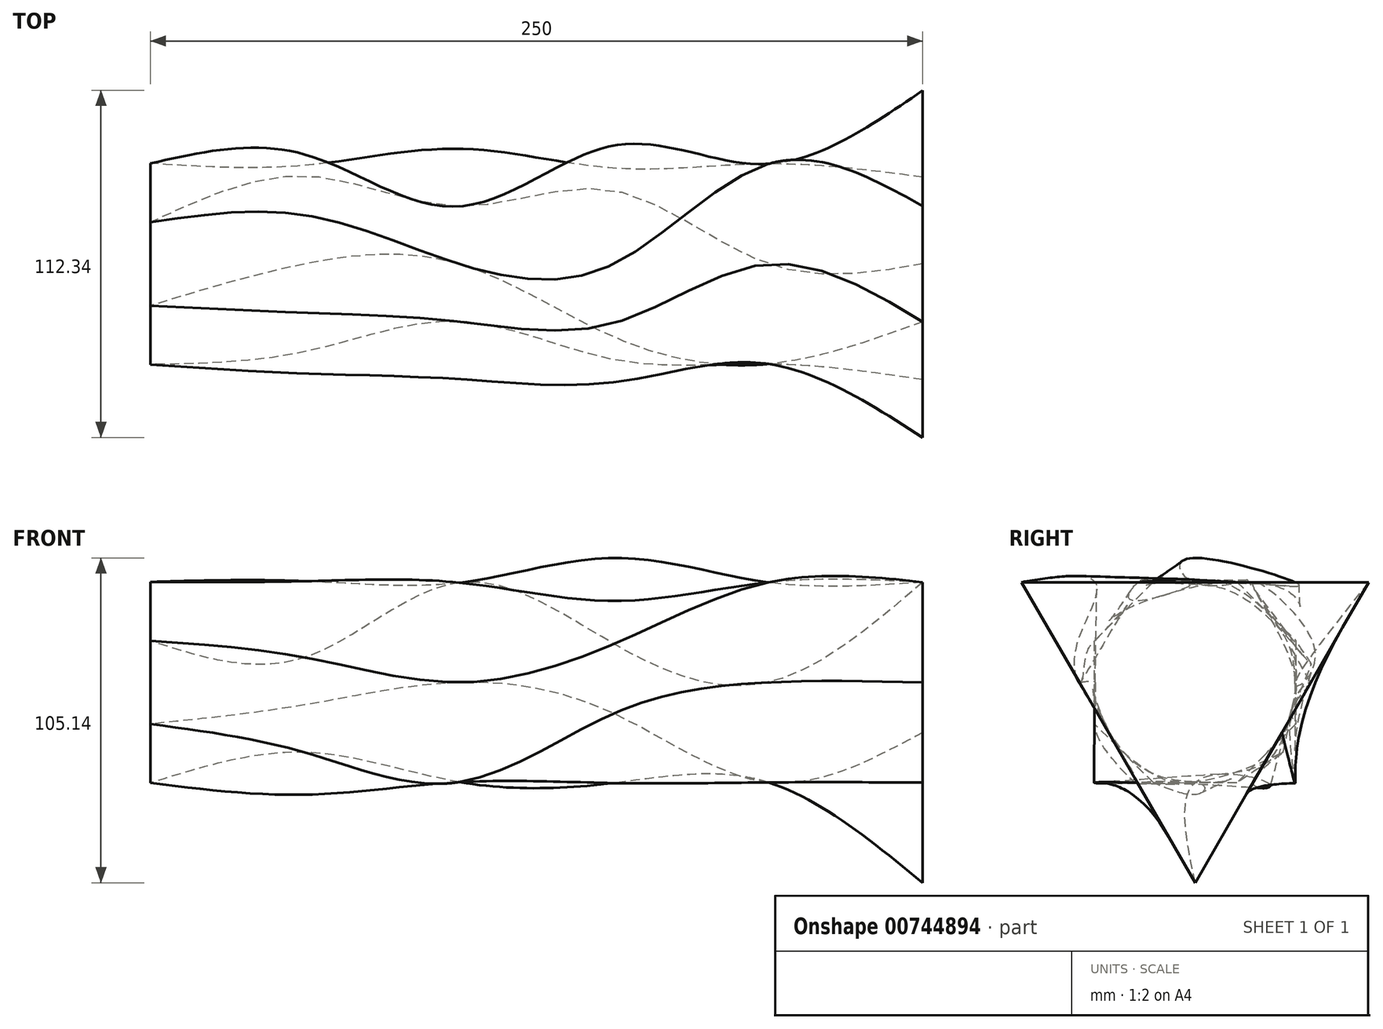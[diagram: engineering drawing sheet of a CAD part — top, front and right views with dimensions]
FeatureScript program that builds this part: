
annotation { "Feature Type Name" : "Feature", "Feature Type Description" : "" }
export const myFeature = defineFeature(function(context is Context, id is Id, definition is map)
    precondition{}
    {
        {
            var Q0;
            Q0=qCreatedBy(makeId("Right.planeOp"),FACE);
            var sketch = newSketch(context, id + "F0", { "sketchPlane" : qUnion([Q0])});
            skCircle(sketch, "E0.cCircle", {"center": v(0, 0) * mm, "radius": 32.43 * mm, "construction": true});
            skLineSegment(sketch, "E0.0", {"start": v(-56.17, 32.43) * mm, "end": v(56.17, 32.43) * mm});
            skLineSegment(sketch, "E0.1", {"start": v(56.17, 32.43) * mm, "end": v(0, -64.86) * mm});
            skLineSegment(sketch, "E0.2", {"start": v(0, -64.86) * mm, "end": v(-56.17, 32.43) * mm});
            skPoint(sketch, "E0.0.midPoint", {"position": v(0, 32.43) * mm});
            skSolve(sketch);
        }
        {
            var Q0;
            Q0=makeQuery(id+"F0.imprint","IMPRINT",FACE,{"disambiguationData":[TD([[makeQuery(id+"F0.imprint","IMPRINT",EDGE,{"derivedFrom":sQuery(id+"F0.wireOp",EDGE,"E0.0")}),-1.0]])]});
            cPlane(context, id + "F1", {"entities" : qUnion([Q0]), "cplaneType" : CPlaneType.OFFSET, "offset" : 50 * mm, "oppositeDirection" : true, "width" : 150 * mm, "height" : 150 * mm});
        }
        {
            var Q0;
            Q0=qCreatedBy(id+"F1.planeOp",FACE);
            var sketch = newSketch(context, id + "F2", { "sketchPlane" : qUnion([Q0])});
            skCircle(sketch, "E1.cCircle", {"center": v(0, 0) * mm, "radius": 32.38 * mm, "construction": true});
            skLineSegment(sketch, "E1.0", {"start": v(-32.38, 32.38) * mm, "end": v(32.38, 32.38) * mm});
            skLineSegment(sketch, "E1.1", {"start": v(32.38, 32.38) * mm, "end": v(32.38, -32.38) * mm});
            skLineSegment(sketch, "E1.2", {"start": v(32.38, -32.38) * mm, "end": v(-32.38, -32.38) * mm});
            skLineSegment(sketch, "E1.3", {"start": v(-32.38, -32.38) * mm, "end": v(-32.38, 32.38) * mm});
            skPoint(sketch, "E1.0.midPoint", {"position": v(0, 32.38) * mm});
            skSolve(sketch);
        }
        {
            var Q0;
            Q0=makeQuery(id+"F2.imprint","IMPRINT",FACE,{"disambiguationData":[TD([[makeQuery(id+"F2.imprint","IMPRINT",EDGE,{"derivedFrom":sQuery(id+"F2.wireOp",EDGE,"E1.0")}),-1.0]])]});
            cPlane(context, id + "F3", {"entities" : qUnion([Q0]), "cplaneType" : CPlaneType.OFFSET, "offset" : 50 * mm, "oppositeDirection" : true, "width" : 150 * mm, "height" : 150 * mm});
        }
        {
            var Q0;
            Q0=qCreatedBy(id+"F3.planeOp",FACE);
            var sketch = newSketch(context, id + "F4", { "sketchPlane" : qUnion([Q0])});
            skCircle(sketch, "E2.cCircle", {"center": v(0, 0) * mm, "radius": 32.59 * mm, "construction": true});
            skLineSegment(sketch, "E2.0", {"start": v(23.68, -32.59) * mm, "end": v(-23.68, -32.59) * mm});
            skLineSegment(sketch, "E2.1", {"start": v(-23.68, -32.59) * mm, "end": v(-38.31, 12.45) * mm});
            skLineSegment(sketch, "E2.2", {"start": v(-38.31, 12.45) * mm, "end": v(0, 40.28) * mm});
            skLineSegment(sketch, "E2.3", {"start": v(0, 40.28) * mm, "end": v(38.31, 12.45) * mm});
            skLineSegment(sketch, "E2.4", {"start": v(38.31, 12.45) * mm, "end": v(23.68, -32.59) * mm});
            skPoint(sketch, "E2.0.midPoint", {"position": v(0, -32.59) * mm});
            skSolve(sketch);
        }
        {
            var Q0;
            Q0=makeQuery(id+"F4.imprint","IMPRINT",FACE,{"disambiguationData":[TD([[makeQuery(id+"F4.imprint","IMPRINT",EDGE,{"derivedFrom":sQuery(id+"F4.wireOp",EDGE,"E2.0")}),-1.0]])]});
            cPlane(context, id + "F5", {"entities" : qUnion([Q0]), "cplaneType" : CPlaneType.OFFSET, "offset" : 50 * mm, "oppositeDirection" : true, "width" : 150 * mm, "height" : 150 * mm});
        }
        {
            var Q0;
            Q0=qCreatedBy(id+"F5.planeOp",FACE);
            var sketch = newSketch(context, id + "F6", { "sketchPlane" : qUnion([Q0])});
            skCircle(sketch, "E3.cCircle", {"center": v(0, 0) * mm, "radius": 32.28 * mm, "construction": true});
            skLineSegment(sketch, "E3.0", {"start": v(-18.64, 32.28) * mm, "end": v(18.64, 32.28) * mm});
            skLineSegment(sketch, "E3.1", {"start": v(18.64, 32.28) * mm, "end": v(37.28, 0) * mm});
            skLineSegment(sketch, "E3.2", {"start": v(37.28, 0) * mm, "end": v(18.64, -32.28) * mm});
            skLineSegment(sketch, "E3.3", {"start": v(18.64, -32.28) * mm, "end": v(-18.64, -32.28) * mm});
            skLineSegment(sketch, "E3.4", {"start": v(-18.64, -32.28) * mm, "end": v(-37.28, 0) * mm});
            skLineSegment(sketch, "E3.5", {"start": v(-37.28, 0) * mm, "end": v(-18.64, 32.28) * mm});
            skPoint(sketch, "E3.0.midPoint", {"position": v(0, 32.28) * mm});
            skSolve(sketch);
        }
        {
            var Q0;
            Q0=makeQuery(id+"F6.imprint","IMPRINT",FACE,{"disambiguationData":[TD([[makeQuery(id+"F6.imprint","IMPRINT",EDGE,{"derivedFrom":sQuery(id+"F6.wireOp",EDGE,"E3.0")}),-1.0]])]});
            cPlane(context, id + "F7", {"entities" : qUnion([Q0]), "cplaneType" : CPlaneType.OFFSET, "offset" : 50 * mm, "oppositeDirection" : true, "width" : 150 * mm, "height" : 150 * mm});
        }
        {
            var Q0;
            Q0=qCreatedBy(id+"F7.planeOp",FACE);
            var sketch = newSketch(context, id + "F8", { "sketchPlane" : qUnion([Q0])});
            skCircle(sketch, "E4.cCircle", {"center": v(0, 0) * mm, "radius": 32.75 * mm, "construction": true});
            skLineSegment(sketch, "E4.0", {"start": v(-15.77, 32.75) * mm, "end": v(15.77, 32.75) * mm});
            skLineSegment(sketch, "E4.1", {"start": v(15.77, 32.75) * mm, "end": v(35.44, 8.09) * mm});
            skLineSegment(sketch, "E4.2", {"start": v(35.44, 8.09) * mm, "end": v(28.42, -22.66) * mm});
            skLineSegment(sketch, "E4.3", {"start": v(28.42, -22.66) * mm, "end": v(0, -36.35) * mm});
            skLineSegment(sketch, "E4.4", {"start": v(0, -36.35) * mm, "end": v(-28.42, -22.66) * mm});
            skLineSegment(sketch, "E4.5", {"start": v(-28.42, -22.66) * mm, "end": v(-35.44, 8.09) * mm});
            skLineSegment(sketch, "E4.6", {"start": v(-35.44, 8.09) * mm, "end": v(-15.77, 32.75) * mm});
            skPoint(sketch, "E4.0.midPoint", {"position": v(0, 32.75) * mm});
            skSolve(sketch);
        }
        {
            var Q0;
            Q0=makeQuery(id+"F8.imprint","IMPRINT",FACE,{"disambiguationData":[TD([[makeQuery(id+"F8.imprint","IMPRINT",EDGE,{"derivedFrom":sQuery(id+"F8.wireOp",EDGE,"E4.0")}),-1.0]])]});
            cPlane(context, id + "F9", {"entities" : qUnion([Q0]), "cplaneType" : CPlaneType.OFFSET, "offset" : 50 * mm, "oppositeDirection" : true, "width" : 150 * mm, "height" : 150 * mm});
        }
        {
            var Q0;
            Q0=qCreatedBy(id+"F9.planeOp",FACE);
            var sketch = newSketch(context, id + "F10", { "sketchPlane" : qUnion([Q0])});
            skCircle(sketch, "E5.cCircle", {"center": v(0, 0) * mm, "radius": 32.55 * mm, "construction": true});
            skLineSegment(sketch, "E5.0", {"start": v(-13.48, 32.55) * mm, "end": v(13.48, 32.55) * mm});
            skLineSegment(sketch, "E5.1", {"start": v(13.48, 32.55) * mm, "end": v(32.55, 13.48) * mm});
            skLineSegment(sketch, "E5.2", {"start": v(32.55, 13.48) * mm, "end": v(32.55, -13.48) * mm});
            skLineSegment(sketch, "E5.3", {"start": v(32.55, -13.48) * mm, "end": v(13.48, -32.55) * mm});
            skLineSegment(sketch, "E5.4", {"start": v(13.48, -32.55) * mm, "end": v(-13.48, -32.55) * mm});
            skLineSegment(sketch, "E5.5", {"start": v(-13.48, -32.55) * mm, "end": v(-32.55, -13.48) * mm});
            skLineSegment(sketch, "E5.6", {"start": v(-32.55, -13.48) * mm, "end": v(-32.55, 13.48) * mm});
            skLineSegment(sketch, "E5.7", {"start": v(-32.55, 13.48) * mm, "end": v(-13.48, 32.55) * mm});
            skPoint(sketch, "E5.0.midPoint", {"position": v(0, 32.55) * mm});
            skSolve(sketch);
        }
        {
            var Q0;
            Q0=makeQuery(id+"F0.imprint","IMPRINT",FACE,{"disambiguationData":[TD([[makeQuery(id+"F0.imprint","IMPRINT",EDGE,{"derivedFrom":sQuery(id+"F0.wireOp",EDGE,"E0.0")}),-1.0]])]});
            var Q1;
            Q1=makeQuery(id+"F2.imprint","IMPRINT",FACE,{"disambiguationData":[TD([[makeQuery(id+"F2.imprint","IMPRINT",EDGE,{"derivedFrom":sQuery(id+"F2.wireOp",EDGE,"E1.0")}),-1.0]])]});
            var Q2;
            Q2=makeQuery(id+"F4.imprint","IMPRINT",FACE,{"disambiguationData":[TD([[makeQuery(id+"F4.imprint","IMPRINT",EDGE,{"derivedFrom":sQuery(id+"F4.wireOp",EDGE,"E2.0")}),-1.0]])]});
            var Q3;
            Q3=makeQuery(id+"F6.imprint","IMPRINT",FACE,{"disambiguationData":[TD([[makeQuery(id+"F6.imprint","IMPRINT",EDGE,{"derivedFrom":sQuery(id+"F6.wireOp",EDGE,"E3.0")}),-1.0]])]});
            var Q4;
            Q4=makeQuery(id+"F8.imprint","IMPRINT",FACE,{"disambiguationData":[TD([[makeQuery(id+"F8.imprint","IMPRINT",EDGE,{"derivedFrom":sQuery(id+"F8.wireOp",EDGE,"E4.0")}),-1.0]])]});
            var Q5;
            Q5=makeQuery(id+"F10.imprint","IMPRINT",FACE,{"disambiguationData":[TD([[makeQuery(id+"F10.imprint","IMPRINT",EDGE,{"derivedFrom":sQuery(id+"F10.wireOp",EDGE,"E5.0")}),-1.0]])]});
            loft(context, id + "F11", {"sheetProfilesArray" : [{ "sheetProfileEntities" : qUnion([Q0]) }, { "sheetProfileEntities" : qUnion([Q1]) }, { "sheetProfileEntities" : qUnion([Q2]) }, { "sheetProfileEntities" : qUnion([Q3]) }, { "sheetProfileEntities" : qUnion([Q4]) }, { "sheetProfileEntities" : qUnion([Q5]) }]});
        }
    });
